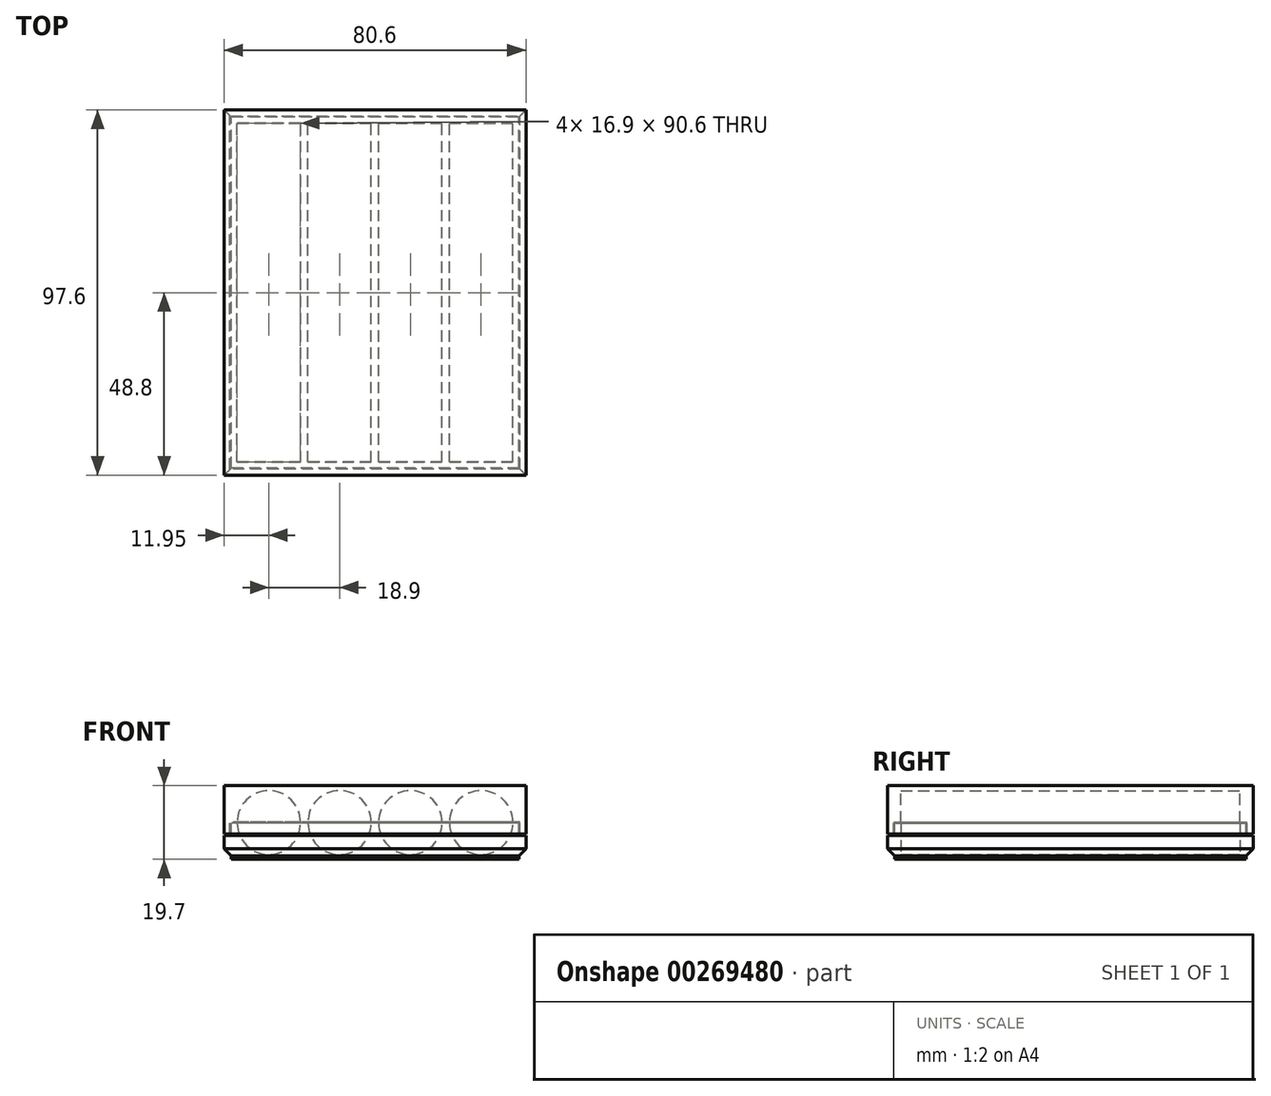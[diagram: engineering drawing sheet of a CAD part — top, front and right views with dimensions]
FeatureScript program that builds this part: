
annotation { "Feature Type Name" : "Feature", "Feature Type Description" : "" }
export const myFeature = defineFeature(function(context is Context, id is Id, definition is map)
    precondition{}
    {
        {
            assignVariable(context, id + "F0", {"name" : "chaff", "anyValue" : .3});
        }
        {
            assignVariable(context, id + "F1", {"name" : "basethick", "anyValue" : 1});
        }
        {
            assignVariable(context, id + "F2", {"name" : "diskdiam", "anyValue" : 16.3});
        }
        {
            var Q0;
            Q0=qCreatedBy(makeId("Top.planeOp"),FACE);
            var sketch = newSketch(context, id + "F3", { "sketchPlane" : qUnion([Q0])});
            skLineSegment(sketch, "E0.bottom", {"start": v(40.3, -48.8) * mm, "end": v(-40.3, -48.8) * mm});
            skLineSegment(sketch, "E0.top", {"start": v(40.3, 48.8) * mm, "end": v(-40.3, 48.8) * mm});
            skLineSegment(sketch, "E0.left", {"start": v(40.3, -48.8) * mm, "end": v(40.3, 48.8) * mm});
            skLineSegment(sketch, "E0.right", {"start": v(-40.3, -48.8) * mm, "end": v(-40.3, 48.8) * mm});
            skPoint(sketch, "E0.middle", {"position": v(0, 0) * mm});
            skSolve(sketch);
        }
        {
            var Q0;
            Q0 = qSketchRegion(id + "F3", true);
            extrude(context, id + "F4", {"entities" : qUnion([Q0]), "depth" : (getVariable(context, 'basethick')) * mm});
        }
        {
            var Q0;
            Q0=makeQuery(id+"F4.opExtrude","CAP_FACE",FACE,{"disambiguationData":[OSD([sQuery(id+"F3.wireOp",EDGE,"E0.bottom"),sQuery(id+"F3.wireOp",EDGE,"E0.top"),sQuery(id+"F3.wireOp",EDGE,"E0.left"),sQuery(id+"F3.wireOp",EDGE,"E0.right")])],"isStart":false});
            var sketch = newSketch(context, id + "F5", { "sketchPlane" : qUnion([Q0])});
            skLineSegment(sketch, "E1.bottom", {"start": v(36.8, -45.3) * mm, "end": v(-36.8, -45.3) * mm});
            skLineSegment(sketch, "E1.top", {"start": v(36.8, 45.3) * mm, "end": v(-36.8, 45.3) * mm});
            skLineSegment(sketch, "E1.left", {"start": v(36.8, -45.3) * mm, "end": v(36.8, 45.3) * mm});
            skLineSegment(sketch, "E1.right", {"start": v(-36.8, -45.3) * mm, "end": v(-36.8, 45.3) * mm});
            skPoint(sketch, "E1.middle", {"position": v(0, 0) * mm});
            skLineSegment(sketch, "E2", {"start": v(-40.3, 0) * mm, "end": v(-36.8, 0) * mm, "construction": true});
            skLineSegment(sketch, "E3", {"start": v(0, 45.3) * mm, "end": v(0, 48.8) * mm, "construction": true});
            skLineSegment(sketch, "E4.0", {"start": v(-40.3, -48.8) * mm, "end": v(-40.3, 48.8) * mm});
            skLineSegment(sketch, "E5.0", {"start": v(40.3, -48.8) * mm, "end": v(-40.3, -48.8) * mm});
            skLineSegment(sketch, "E6.0", {"start": v(40.3, -48.8) * mm, "end": v(40.3, 48.8) * mm});
            skLineSegment(sketch, "E7.0", {"start": v(40.3, 48.8) * mm, "end": v(-40.3, 48.8) * mm});
            skSolve(sketch);
        }
        {
            var Q0;
            Q0 = qSketchRegion(id + "F5", true);
            extrude(context, id + "F6", {"entities" : qUnion([Q0]), "operationType" : NewBodyOperationType.ADD, "depth" : (getVariable(context, 'diskdiam') / 2 + getVariable(context, 'chaff') * 2) * mm});
        }
        {
            var Q0;
            Q0=makeQuery(id+"F6.opExtrude","SWEPT_FACE",FACE,{"disambiguationData":[OSD([sQuery(id+"F5.wireOp",EDGE,"E1.top")])]});
            var sketch = newSketch(context, id + "F7", { "sketchPlane" : qUnion([Q0])});
            skLineSegment(sketch, "E8", {"start": v(-36.8, 9.75) * mm, "end": v(-19.9, 9.75) * mm});
            skArc(sketch, "E9", {"start": v(-36.8, 9.75) * mm, "mid": v(-28.35, 1.3) * mm, "end": v(-19.9, 9.75) * mm});
            skLineSegment(sketch, "E10.1.0.0", {"start": v(-17.9, 9.75) * mm, "end": v(-1, 9.75) * mm});
            skArc(sketch, "E10.1.0.1", {"start": v(-17.9, 9.75) * mm, "mid": v(-9.45, 1.3) * mm, "end": v(-1, 9.75) * mm});
            skLineSegment(sketch, "E10.2.0.0", {"start": v(1, 9.75) * mm, "end": v(17.9, 9.75) * mm});
            skArc(sketch, "E10.2.0.1", {"start": v(1, 9.75) * mm, "mid": v(9.45, 1.3) * mm, "end": v(17.9, 9.75) * mm});
            skLineSegment(sketch, "E10.3.0.0", {"start": v(19.9, 9.75) * mm, "end": v(36.8, 9.75) * mm});
            skArc(sketch, "E10.3.0.1", {"start": v(19.9, 9.75) * mm, "mid": v(28.35, 1.3) * mm, "end": v(36.8, 9.75) * mm});
            skLineSegment(sketch, "E10.direction1", {"start": v(-36.8, 9.75) * mm, "end": v(-17.9, 9.75) * mm, "construction": true});
            skLineSegment(sketch, "E11.0", {"start": v(36.8, 1) * mm, "end": v(-36.8, 1) * mm});
            skLineSegment(sketch, "E12.0", {"start": v(-36.8, 9.75) * mm, "end": v(-36.8, 1) * mm});
            skLineSegment(sketch, "E13.0", {"start": v(36.8, 9.75) * mm, "end": v(36.8, 1) * mm});
            skLineSegment(sketch, "E14.0", {"start": v(36.8, 9.75) * mm, "end": v(-36.8, 9.75) * mm});
            skSolve(sketch);
        }
        {
            var Q0;
            {var subQ5=sQuery(id+"F7.wireOp",EDGE,"E9");Q0=makeQuery(id+"F7.imprint","IMPRINT",FACE,{"disambiguationData":[TD([[makeQuery(id+"F7.imprint","IMPRINT",EDGE,{"derivedFrom":subQ5}),-1.0]])]});}
            var Q1;
            Q1=makeQuery(id+"F6.opExtrude","SWEPT_FACE",FACE,{"disambiguationData":[OSD([sQuery(id+"F5.wireOp",EDGE,"E1.bottom")])]});
            extrude(context, id + "F8", {"entities" : qUnion([Q0]), "operationType" : NewBodyOperationType.ADD, "endBound" : BoundingType.UP_TO_SURFACE, "endBoundEntityFace" : qUnion([Q1]), "depth" : 25 * mm});
        }
        {
            var Q0;
            {var subQ0=sQuery(id+"F7.wireOp",EDGE,"E14.0");var subQ1=sQuery(id+"F7.wireOp",EDGE,"E10.1.0.1");var subQ2=sQuery(id+"F7.wireOp",EDGE,"E10.2.0.1");Q0=makeQuery(id+"F8.boolean.opBoolean","MERGE",FACE,{"derivedFrom":[makeQuery(id+"F6.opExtrude","CAP_FACE",FACE,{"disambiguationData":[OSD([sQuery(id+"F5.wireOp",EDGE,"E1.bottom"),sQuery(id+"F5.wireOp",EDGE,"E1.top"),sQuery(id+"F5.wireOp",EDGE,"E1.left"),sQuery(id+"F5.wireOp",EDGE,"E1.right"),sQuery(id+"F5.wireOp",EDGE,"E4.0"),sQuery(id+"F5.wireOp",EDGE,"E5.0"),sQuery(id+"F5.wireOp",EDGE,"E6.0"),sQuery(id+"F5.wireOp",EDGE,"E7.0")])],"isStart":false}),makeQuery(id+"F8.opExtrude","SWEPT_FACE",FACE,{"disambiguationData":[OSD([subQ0]),TDD([makeQuery(id+"F7.imprint","IMPRINT",EDGE,{"disambiguationData":[TD([[makeQuery(id+"F7.imprint","INTERSECT",VERTEX,{"derivedFrom":[sQuery(id+"F7.wireOp",EDGE,"E13.0"),subQ0]}),-1.0]])],"derivedFrom":subQ0})])]}),makeQuery(id+"F8.opExtrude","SWEPT_FACE",FACE,{"disambiguationData":[OSD([subQ0]),TDD([makeQuery(id+"F7.imprint","IMPRINT",EDGE,{"disambiguationData":[TD([[makeQuery(id+"F7.imprint","INTERSECT",VERTEX,{"disambiguationData":[OD(1.0)],"derivedFrom":[subQ2,subQ0]}),1.0]])],"derivedFrom":subQ0})])]}),makeQuery(id+"F8.opExtrude","SWEPT_FACE",FACE,{"disambiguationData":[OSD([subQ0]),TDD([makeQuery(id+"F7.imprint","IMPRINT",EDGE,{"disambiguationData":[TD([[makeQuery(id+"F7.imprint","INTERSECT",VERTEX,{"disambiguationData":[OD(1.0)],"derivedFrom":[subQ1,subQ0]}),1.0]])],"derivedFrom":subQ0})])]}),makeQuery(id+"F8.opExtrude","SWEPT_FACE",FACE,{"disambiguationData":[OSD([subQ0]),TDD([makeQuery(id+"F7.imprint","IMPRINT",EDGE,{"disambiguationData":[TD([[makeQuery(id+"F7.imprint","INTERSECT",VERTEX,{"derivedFrom":[sQuery(id+"F7.wireOp",EDGE,"E9"),subQ0]}),1.0]])],"derivedFrom":subQ0})])]})]});}
            cPlane(context, id + "F9", {"entities" : qUnion([Q0]), "cplaneType" : CPlaneType.OFFSET, "offset" : .1 * mm, "width" : 150 * mm, "height" : 150 * mm});
        }
        {
            var Q0;
            Q0=makeQuery(id+"F4.opExtrude","SWEPT_BODY",BODY,{"disambiguationData":[OSD([sQuery(id+"F3.wireOp",EDGE,"E0.bottom"),sQuery(id+"F3.wireOp",EDGE,"E0.top"),sQuery(id+"F3.wireOp",EDGE,"E0.left"),sQuery(id+"F3.wireOp",EDGE,"E0.right")])]});
            var Q1;
            Q1=qCreatedBy(id+"F9.planeOp",FACE);
            mirror(context, id + "F10", {"entities" : qUnion([Q0]), "mirrorPlane" : qUnion([Q1])});
        }
        {
            var Q0;
            {var subQ0=sQuery(id+"F7.wireOp",EDGE,"E14.0");var subQ1=sQuery(id+"F7.wireOp",EDGE,"E10.1.0.1");var subQ2=sQuery(id+"F7.wireOp",EDGE,"E10.2.0.1");Q0=makeQuery(id+"F8.boolean.opBoolean","MERGE",FACE,{"derivedFrom":[makeQuery(id+"F6.opExtrude","CAP_FACE",FACE,{"disambiguationData":[OSD([sQuery(id+"F5.wireOp",EDGE,"E1.bottom"),sQuery(id+"F5.wireOp",EDGE,"E1.top"),sQuery(id+"F5.wireOp",EDGE,"E1.left"),sQuery(id+"F5.wireOp",EDGE,"E1.right"),sQuery(id+"F5.wireOp",EDGE,"E4.0"),sQuery(id+"F5.wireOp",EDGE,"E5.0"),sQuery(id+"F5.wireOp",EDGE,"E6.0"),sQuery(id+"F5.wireOp",EDGE,"E7.0")])],"isStart":false}),makeQuery(id+"F8.opExtrude","SWEPT_FACE",FACE,{"disambiguationData":[OSD([subQ0]),TDD([makeQuery(id+"F7.imprint","IMPRINT",EDGE,{"disambiguationData":[TD([[makeQuery(id+"F7.imprint","INTERSECT",VERTEX,{"derivedFrom":[sQuery(id+"F7.wireOp",EDGE,"E13.0"),subQ0]}),-1.0]])],"derivedFrom":subQ0})])]}),makeQuery(id+"F8.opExtrude","SWEPT_FACE",FACE,{"disambiguationData":[OSD([subQ0]),TDD([makeQuery(id+"F7.imprint","IMPRINT",EDGE,{"disambiguationData":[TD([[makeQuery(id+"F7.imprint","INTERSECT",VERTEX,{"disambiguationData":[OD(1.0)],"derivedFrom":[subQ2,subQ0]}),1.0]])],"derivedFrom":subQ0})])]}),makeQuery(id+"F8.opExtrude","SWEPT_FACE",FACE,{"disambiguationData":[OSD([subQ0]),TDD([makeQuery(id+"F7.imprint","IMPRINT",EDGE,{"disambiguationData":[TD([[makeQuery(id+"F7.imprint","INTERSECT",VERTEX,{"disambiguationData":[OD(1.0)],"derivedFrom":[subQ1,subQ0]}),1.0]])],"derivedFrom":subQ0})])]}),makeQuery(id+"F8.opExtrude","SWEPT_FACE",FACE,{"disambiguationData":[OSD([subQ0]),TDD([makeQuery(id+"F7.imprint","IMPRINT",EDGE,{"disambiguationData":[TD([[makeQuery(id+"F7.imprint","INTERSECT",VERTEX,{"derivedFrom":[sQuery(id+"F7.wireOp",EDGE,"E9"),subQ0]}),1.0]])],"derivedFrom":subQ0})])]})]});}
            var sketch = newSketch(context, id + "F11", { "sketchPlane" : qUnion([Q0])});
            skLineSegment(sketch, "E15.0", {"start": v(40.3, 48.8) * mm, "end": v(-40.3, 48.8) * mm});
            skLineSegment(sketch, "E16.0", {"start": v(-40.3, -48.8) * mm, "end": v(-40.3, 48.8) * mm});
            skLineSegment(sketch, "E17.0", {"start": v(40.3, -48.8) * mm, "end": v(-40.3, -48.8) * mm});
            skLineSegment(sketch, "E18.0", {"start": v(40.3, -48.8) * mm, "end": v(40.3, 48.8) * mm});
            skLineSegment(sketch, "E19.0", {"start": v(38.4, 46.9) * mm, "end": v(-38.4, 46.9) * mm});
            skLineSegment(sketch, "E19.1", {"start": v(38.4, -46.9) * mm, "end": v(38.4, 46.9) * mm});
            skLineSegment(sketch, "E19.2", {"start": v(38.4, -46.9) * mm, "end": v(-38.4, -46.9) * mm});
            skLineSegment(sketch, "E19.3", {"start": v(-38.4, -46.9) * mm, "end": v(-38.4, 46.9) * mm});
            skSolve(sketch);
        }
        {
            assignVariable(context, id + "F12", {"name" : "lidrimdepth", "anyValue" : 3});
        }
        {
            var Q0;
            Q0=makeQuery(id+"F11.imprint","IMPRINT",FACE,{"disambiguationData":[TD([[makeQuery(id+"F11.imprint","IMPRINT",EDGE,{"derivedFrom":sQuery(id+"F11.wireOp",EDGE,"E15.0")}),1.0]])]});
            extrude(context, id + "F13", {"entities" : qUnion([Q0]), "operationType" : NewBodyOperationType.REMOVE, "oppositeDirection" : true, "depth" : (getVariable(context, 'lidrimdepth') + getVariable(context, 'chaff')) * mm});
        }
        {
            var Q0;
            Q0=makeQuery(id+"F4.opExtrude","CAP_FACE",FACE,{"disambiguationData":[OSD([sQuery(id+"F3.wireOp",EDGE,"E0.bottom"),sQuery(id+"F3.wireOp",EDGE,"E0.top"),sQuery(id+"F3.wireOp",EDGE,"E0.left"),sQuery(id+"F3.wireOp",EDGE,"E0.right")])],"isStart":true});
            var sketch = newSketch(context, id + "F14", { "sketchPlane" : qUnion([Q0])});
            skLineSegment(sketch, "E20.0", {"start": v(40.3, 48.8) * mm, "end": v(-40.3, 48.8) * mm});
            skLineSegment(sketch, "E21.0", {"start": v(-40.3, 48.8) * mm, "end": v(-40.3, -48.8) * mm});
            skLineSegment(sketch, "E22.0", {"start": v(40.3, 48.8) * mm, "end": v(40.3, -48.8) * mm});
            skLineSegment(sketch, "E23.0", {"start": v(40.3, -48.8) * mm, "end": v(-40.3, -48.8) * mm});
            skLineSegment(sketch, "E24.0", {"start": v(38.4, 46.9) * mm, "end": v(-38.4, 46.9) * mm});
            skLineSegment(sketch, "E24.1", {"start": v(38.4, 46.9) * mm, "end": v(38.4, -46.9) * mm});
            skLineSegment(sketch, "E24.2", {"start": v(38.4, -46.9) * mm, "end": v(-38.4, -46.9) * mm});
            skLineSegment(sketch, "E24.3", {"start": v(-38.4, 46.9) * mm, "end": v(-38.4, -46.9) * mm});
            skSolve(sketch);
        }
        {
            var Q0;
            Q0 = qSketchRegion(id + "F14", true);
            extrude(context, id + "F15", {"entities" : qUnion([Q0]), "operationType" : NewBodyOperationType.REMOVE, "oppositeDirection" : true, "depth" : (getVariable(context, 'lidrimdepth')) * mm});
        }
        {
            var Q0;
            Q0=makeQuery(id+"F15.boolean.opBoolean","COPY",EDGE,{"derivedFrom":makeQuery(id+"F15.opExtrude","CAP_EDGE",EDGE,{"disambiguationData":[OSD([sQuery(id+"F14.wireOp",EDGE,"E24.0")])],"isStart":false})});
            var Q1;
            Q1=makeQuery(id+"F15.boolean.opBoolean","COPY",EDGE,{"derivedFrom":makeQuery(id+"F15.opExtrude","CAP_EDGE",EDGE,{"disambiguationData":[OSD([sQuery(id+"F14.wireOp",EDGE,"E24.3")])],"isStart":false})});
            var Q2;
            Q2=makeQuery(id+"F15.boolean.opBoolean","COPY",EDGE,{"derivedFrom":makeQuery(id+"F15.opExtrude","CAP_EDGE",EDGE,{"disambiguationData":[OSD([sQuery(id+"F14.wireOp",EDGE,"E24.2")])],"isStart":false})});
            var Q3;
            Q3=makeQuery(id+"F15.boolean.opBoolean","COPY",EDGE,{"derivedFrom":makeQuery(id+"F15.opExtrude","CAP_EDGE",EDGE,{"disambiguationData":[OSD([sQuery(id+"F14.wireOp",EDGE,"E24.1")])],"isStart":false})});
            chamfer(context, id + "F16", {"entities" : qUnion([Q0, Q1, Q2, Q3]), "width" : 2 * mm, "tangentPropagation" : true});
        }
        {
            var Q0;
            {var subQ0=sQuery(id+"F7.wireOp",EDGE,"E14.0");var subQ1=sQuery(id+"F7.wireOp",EDGE,"E10.1.0.1");var subQ2=sQuery(id+"F7.wireOp",EDGE,"E10.2.0.1");Q0=makeQuery(id+"F10.opPattern","COPY",FACE,{"derivedFrom":makeQuery(id+"F8.boolean.opBoolean","MERGE",FACE,{"derivedFrom":[makeQuery(id+"F6.opExtrude","CAP_FACE",FACE,{"disambiguationData":[OSD([sQuery(id+"F5.wireOp",EDGE,"E1.bottom"),sQuery(id+"F5.wireOp",EDGE,"E1.top"),sQuery(id+"F5.wireOp",EDGE,"E1.left"),sQuery(id+"F5.wireOp",EDGE,"E1.right"),sQuery(id+"F5.wireOp",EDGE,"E4.0"),sQuery(id+"F5.wireOp",EDGE,"E5.0"),sQuery(id+"F5.wireOp",EDGE,"E6.0"),sQuery(id+"F5.wireOp",EDGE,"E7.0")])],"isStart":false}),makeQuery(id+"F8.opExtrude","SWEPT_FACE",FACE,{"disambiguationData":[OSD([subQ0]),TDD([makeQuery(id+"F7.imprint","IMPRINT",EDGE,{"disambiguationData":[TD([[makeQuery(id+"F7.imprint","INTERSECT",VERTEX,{"derivedFrom":[sQuery(id+"F7.wireOp",EDGE,"E13.0"),subQ0]}),-1.0]])],"derivedFrom":subQ0})])]}),makeQuery(id+"F8.opExtrude","SWEPT_FACE",FACE,{"disambiguationData":[OSD([subQ0]),TDD([makeQuery(id+"F7.imprint","IMPRINT",EDGE,{"disambiguationData":[TD([[makeQuery(id+"F7.imprint","INTERSECT",VERTEX,{"disambiguationData":[OD(1.0)],"derivedFrom":[subQ2,subQ0]}),1.0]])],"derivedFrom":subQ0})])]}),makeQuery(id+"F8.opExtrude","SWEPT_FACE",FACE,{"disambiguationData":[OSD([subQ0]),TDD([makeQuery(id+"F7.imprint","IMPRINT",EDGE,{"disambiguationData":[TD([[makeQuery(id+"F7.imprint","INTERSECT",VERTEX,{"disambiguationData":[OD(1.0)],"derivedFrom":[subQ1,subQ0]}),1.0]])],"derivedFrom":subQ0})])]}),makeQuery(id+"F8.opExtrude","SWEPT_FACE",FACE,{"disambiguationData":[OSD([subQ0]),TDD([makeQuery(id+"F7.imprint","IMPRINT",EDGE,{"disambiguationData":[TD([[makeQuery(id+"F7.imprint","INTERSECT",VERTEX,{"derivedFrom":[sQuery(id+"F7.wireOp",EDGE,"E9"),subQ0]}),1.0]])],"derivedFrom":subQ0})])]})]}),"instanceName":"1"});}
            var sketch = newSketch(context, id + "F17", { "sketchPlane" : qUnion([Q0])});
            skPoint(sketch, "E25.0", {"position": v(-36.8, 45.3) * mm});
            skPoint(sketch, "E26.0", {"position": v(-36.8, -45.3) * mm});
            skLineSegment(sketch, "E27", {"start": v(-36.8, 45.3) * mm, "end": v(-36.8, -45.3) * mm, "construction": true});
            skLineSegment(sketch, "E28.0", {"start": v(38.7, 47.2) * mm, "end": v(-38.7, 47.2) * mm});
            skLineSegment(sketch, "E28.1", {"start": v(38.7, 47.2) * mm, "end": v(38.7, -47.2) * mm});
            skLineSegment(sketch, "E28.2", {"start": v(-38.7, -47.2) * mm, "end": v(38.7, -47.2) * mm});
            skLineSegment(sketch, "E28.3", {"start": v(-38.7, 47.2) * mm, "end": v(-38.7, -47.2) * mm});
            skLineSegment(sketch, "E29.0", {"start": v(40.3, 48.8) * mm, "end": v(-40.3, 48.8) * mm});
            skLineSegment(sketch, "E30.0", {"start": v(40.3, 48.8) * mm, "end": v(40.3, -48.8) * mm});
            skLineSegment(sketch, "E31.0", {"start": v(40.3, -48.8) * mm, "end": v(-40.3, -48.8) * mm});
            skLineSegment(sketch, "E32.0", {"start": v(-40.3, 48.8) * mm, "end": v(-40.3, -48.8) * mm});
            skPoint(sketch, "E33", {"position": v(36.8, 45.3) * mm});
            skPoint(sketch, "E34", {"position": v(36.8, -45.3) * mm});
            skLineSegment(sketch, "E35", {"start": v(-36.8, 45.3) * mm, "end": v(36.8, 45.3) * mm, "construction": true});
            skLineSegment(sketch, "E36", {"start": v(-36.8, -45.3) * mm, "end": v(36.8, -45.3) * mm, "construction": true});
            skLineSegment(sketch, "E37", {"start": v(0, 47.2) * mm, "end": v(0, 45.3) * mm, "construction": true});
            skLineSegment(sketch, "E38", {"start": v(-38.7, 0) * mm, "end": v(-36.8, 0) * mm, "construction": true});
            skSolve(sketch);
        }
        {
            var Q0;
            Q0 = qSketchRegion(id + "F17", true);
            extrude(context, id + "F18", {"entities" : qUnion([Q0]), "operationType" : NewBodyOperationType.ADD, "depth" : 3.2 * mm});
        }
    });
